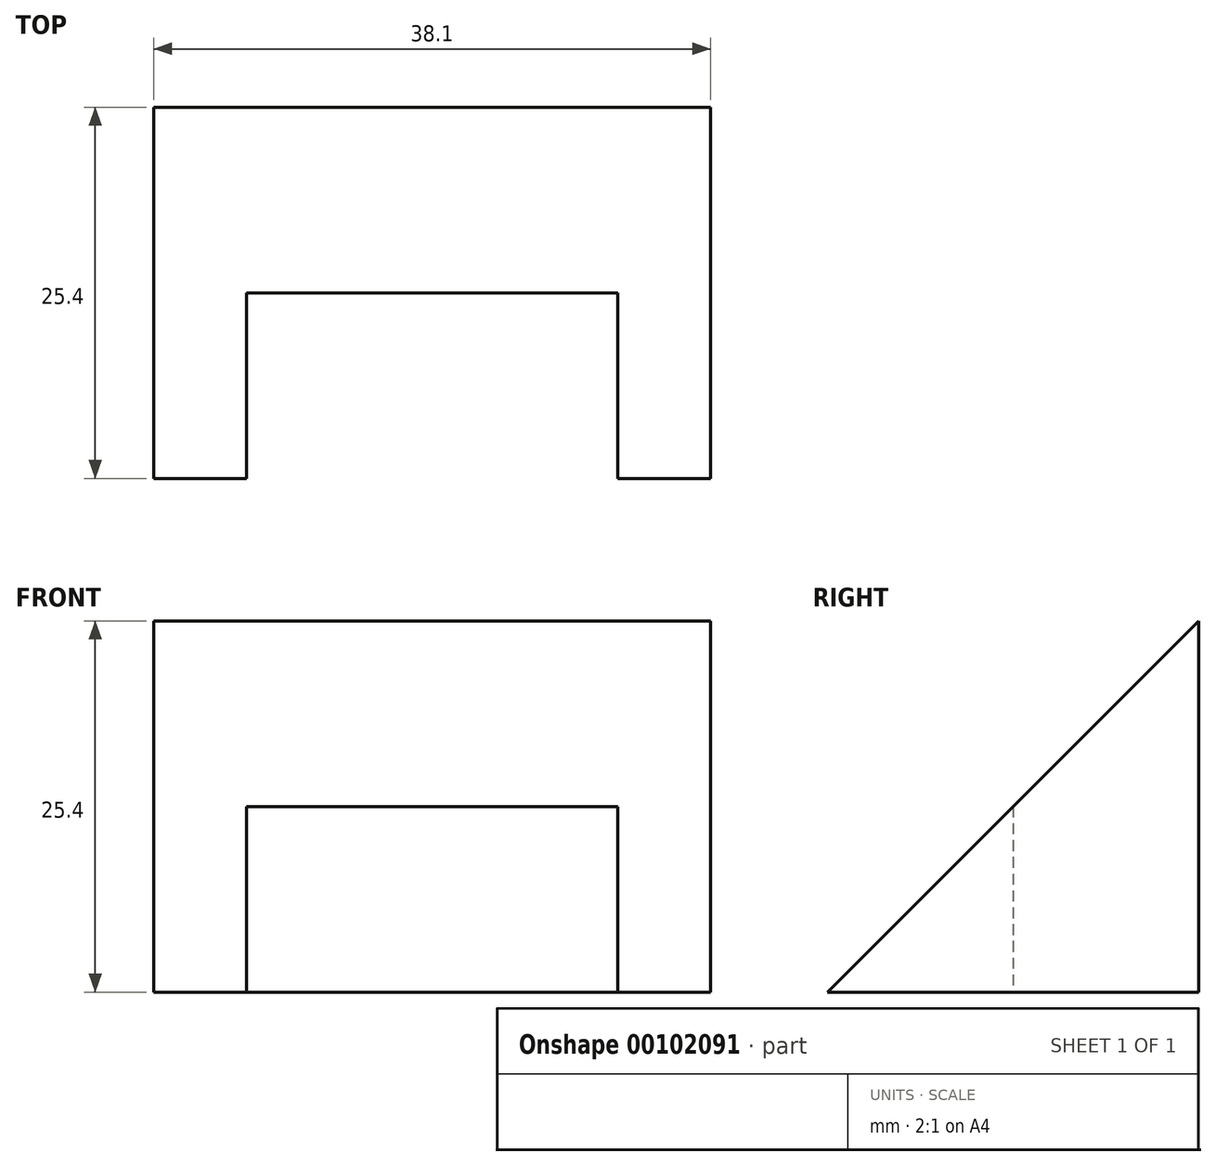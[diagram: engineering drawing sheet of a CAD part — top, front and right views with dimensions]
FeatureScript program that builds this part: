
annotation { "Feature Type Name" : "Feature", "Feature Type Description" : "" }
export const myFeature = defineFeature(function(context is Context, id is Id, definition is map)
    precondition{}
    {
        {
            var Q0;
            Q0=qCreatedBy(makeId("Right.planeOp"),FACE);
            var sketch = newSketch(context, id + "F0", { "sketchPlane" : qUnion([Q0])});
            skLineSegment(sketch, "E0", {"start": v(0, 0) * mm, "end": v(0, 25.4) * mm});
            skLineSegment(sketch, "E1", {"start": v(0, 25.4) * mm, "end": v(-25.4, 0) * mm});
            skLineSegment(sketch, "E2", {"start": v(-25.4, 0) * mm, "end": v(0, 0) * mm});
            skSolve(sketch);
        }
        {
            var Q0;
            Q0 = qSketchRegion(id + "F0", true);
            extrude(context, id + "F1", {"entities" : qUnion([Q0]), "endBound" : BoundingType.SYMMETRIC, "depth" : 38.1 * mm});
        }
        {
            var Q0;
            Q0=makeQuery(id+"F1.opExtrude","CAP_FACE",FACE,{"disambiguationData":[OSD([sQuery(id+"F0.wireOp",EDGE,"E0"),sQuery(id+"F0.wireOp",EDGE,"E1"),sQuery(id+"F0.wireOp",EDGE,"E2")])],"isStart":false});
            var sketch = newSketch(context, id + "F2", { "sketchPlane" : qUnion([Q0])});
            skLineSegment(sketch, "E3", {"start": v(-12.7, 12.7) * mm, "end": v(-12.7, 0) * mm});
            skLineSegment(sketch, "E4", {"start": v(-12.7, 0) * mm, "end": v(-25.4, 0) * mm});
            skLineSegment(sketch, "E5", {"start": v(-25.4, 0) * mm, "end": v(-12.7, 12.7) * mm});
            skSolve(sketch);
        }
        {
            var Q0;
            Q0=makeQuery(id+"F2.imprint","IMPRINT",FACE,{"disambiguationData":[TD([[makeQuery(id+"F2.imprint","IMPRINT",EDGE,{"derivedFrom":sQuery(id+"F2.wireOp",EDGE,"E3")}),-1.0]])]});
            extrude(context, id + "F3", {"entities" : qUnion([Q0]), "operationType" : NewBodyOperationType.REMOVE, "oppositeDirection" : true, "depth" : 31.75 * mm, "hasSecondDirection" : true, "secondDirectionOppositeDirection" : true, "secondDirectionDepth" : 6.35 * mm});
        }
    });
